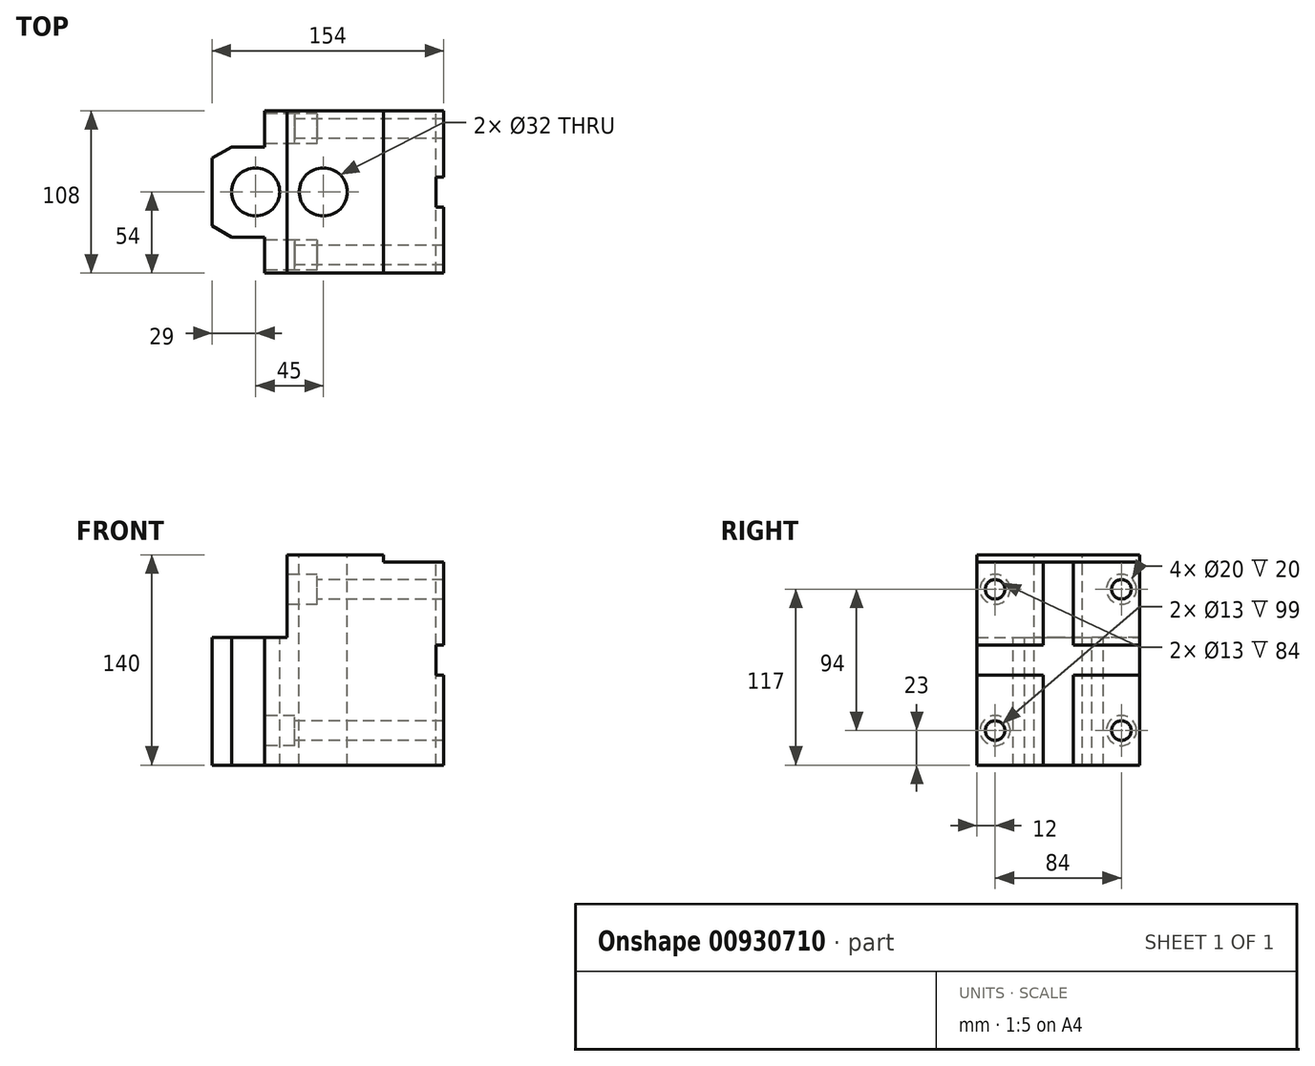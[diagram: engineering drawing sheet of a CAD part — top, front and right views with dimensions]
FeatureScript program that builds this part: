
annotation { "Feature Type Name" : "Feature", "Feature Type Description" : "" }
export const myFeature = defineFeature(function(context is Context, id is Id, definition is map)
    precondition{}
    {
        {
            var Q0;
            Q0=qCreatedBy(makeId("Right.planeOp"),FACE);
            var sketch = newSketch(context, id + "F0", { "sketchPlane" : qUnion([Q0])});
            skLineSegment(sketch, "E0.bottom", {"start": v(54, 70) * mm, "end": v(-54, 70) * mm});
            skLineSegment(sketch, "E0.top", {"start": v(54, -70) * mm, "end": v(-54, -70) * mm});
            skLineSegment(sketch, "E0.left", {"start": v(54, 70) * mm, "end": v(54, -70) * mm});
            skLineSegment(sketch, "E0.right", {"start": v(-54, 70) * mm, "end": v(-54, -70) * mm});
            skPoint(sketch, "E0.middle", {"position": v(0, 0) * mm});
            skSolve(sketch);
        }
        {
            var Q0;
            Q0 = qSketchRegion(id + "F0", true);
            extrude(context, id + "F1", {"entities" : qUnion([Q0]), "oppositeDirection" : true, "depth" : 154 * mm, "offsetDistance" : 25 * mm});
        }
        {
            var Q0;
            Q0=makeQuery(id+"F1.opExtrude","CAP_FACE",FACE,{"disambiguationData":[OSD([sQuery(id+"F0.wireOp",EDGE,"E0.bottom"),sQuery(id+"F0.wireOp",EDGE,"E0.top"),sQuery(id+"F0.wireOp",EDGE,"E0.left"),sQuery(id+"F0.wireOp",EDGE,"E0.right")])],"isStart":false});
            var sketch = newSketch(context, id + "F2", { "sketchPlane" : qUnion([Q0])});
            skCircle(sketch, "E1", {"center": v(-42, 47) * mm, "radius": 6.5 * mm});
            skCircle(sketch, "E2.MirrorC", {"center": v(42, 47) * mm, "radius": 6.5 * mm});
            skCircle(sketch, "E3.MirrorC", {"center": v(-42, -47) * mm, "radius": 6.5 * mm});
            skCircle(sketch, "E4.MirrorC", {"center": v(42, -47) * mm, "radius": 6.5 * mm});
            skSolve(sketch);
        }
        {
            var Q0;
            Q0 = qSketchRegion(id + "F2", true);
            extrude(context, id + "F3", {"entities" : qUnion([Q0]), "operationType" : NewBodyOperationType.REMOVE, "endBound" : BoundingType.THROUGH_ALL, "oppositeDirection" : true, "depth" : 25 * mm, "offsetDistance" : 25 * mm});
        }
        {
            var Q0;
            Q0=makeQuery(id+"F1.opExtrude","SWEPT_FACE",FACE,{"disambiguationData":[OSD([sQuery(id+"F0.wireOp",EDGE,"E0.top")])]});
            var sketch = newSketch(context, id + "F4", { "sketchPlane" : qUnion([Q0])});
            skCircle(sketch, "E5", {"center": v(-125, 0) * mm, "radius": 16 * mm});
            skCircle(sketch, "E6", {"center": v(-80, 0) * mm, "radius": 16 * mm});
            skSolve(sketch);
        }
        {
            var Q0;
            Q0 = qSketchRegion(id + "F4", true);
            extrude(context, id + "F5", {"entities" : qUnion([Q0]), "operationType" : NewBodyOperationType.REMOVE, "endBound" : BoundingType.THROUGH_ALL, "oppositeDirection" : true, "depth" : 25 * mm, "offsetDistance" : 25 * mm});
        }
        {
            var Q0;
            Q0=makeQuery(id+"F1.opExtrude","CAP_FACE",FACE,{"disambiguationData":[OSD([sQuery(id+"F0.wireOp",EDGE,"E0.bottom"),sQuery(id+"F0.wireOp",EDGE,"E0.top"),sQuery(id+"F0.wireOp",EDGE,"E0.left"),sQuery(id+"F0.wireOp",EDGE,"E0.right")])],"isStart":false});
            var sketch = newSketch(context, id + "F6", { "sketchPlane" : qUnion([Q0])});
            skLineSegment(sketch, "E7.bottom", {"start": v(-54, -70) * mm, "end": v(54, -70) * mm});
            skLineSegment(sketch, "E7.top", {"start": v(-54, -15) * mm, "end": v(54, -15) * mm});
            skLineSegment(sketch, "E7.left", {"start": v(-54, -70) * mm, "end": v(-54, -15) * mm});
            skLineSegment(sketch, "E7.right", {"start": v(54, -70) * mm, "end": v(54, -15) * mm});
            skSolve(sketch);
        }
        {
            var Q0;
            Q0 = qSketchRegion(id + "F6", true);
            extrude(context, id + "F7", {"entities" : qUnion([Q0]), "operationType" : NewBodyOperationType.REMOVE, "oppositeDirection" : true, "depth" : 50 * mm, "offsetDistance" : 25 * mm});
        }
        {
            var Q0;
            Q0=makeQuery(id+"F7.boolean.opBoolean","COPY",FACE,{"derivedFrom":makeQuery(id+"F7.opExtrude","SWEPT_FACE",FACE,{"disambiguationData":[OSD([sQuery(id+"F6.wireOp",EDGE,"E7.top")])]})});
            var sketch = newSketch(context, id + "F8", { "sketchPlane" : qUnion([Q0])});
            skLineSegment(sketch, "E8", {"start": v(-104, 54) * mm, "end": v(-119, 54) * mm});
            skLineSegment(sketch, "E9", {"start": v(-119, 54) * mm, "end": v(-119, 30) * mm});
            skLineSegment(sketch, "E10", {"start": v(-119, 30) * mm, "end": v(-141, 30) * mm});
            skLineSegment(sketch, "E11", {"start": v(-141, 30) * mm, "end": v(-154, 22.5) * mm});
            skLineSegment(sketch, "E12", {"start": v(-154, 22.5) * mm, "end": v(-154, 0) * mm});
            skLineSegment(sketch, "E13", {"start": v(-104, 54) * mm, "end": v(-104, 0) * mm});
            skLineSegment(sketch, "E14.MirrorCS", {"start": v(-154, -22.5) * mm, "end": v(-154, 0) * mm});
            skLineSegment(sketch, "E15.MirrorCS", {"start": v(-141, -30) * mm, "end": v(-154, -22.5) * mm});
            skLineSegment(sketch, "E16.MirrorCS", {"start": v(-119, -30) * mm, "end": v(-141, -30) * mm});
            skLineSegment(sketch, "E17.MirrorCS", {"start": v(-119, -54) * mm, "end": v(-119, -30) * mm});
            skLineSegment(sketch, "E18.MirrorCS", {"start": v(-104, -54) * mm, "end": v(-119, -54) * mm});
            skLineSegment(sketch, "E19.MirrorCS", {"start": v(-104, -54) * mm, "end": v(-104, 0) * mm});
            skSolve(sketch);
        }
        {
            var Q0;
            {var subQ5=sQuery(id+"F8.wireOp",EDGE,"E15.MirrorCS");Q0=makeQuery(id+"F8.imprint","IMPRINT",FACE,{"disambiguationData":[TD([[makeQuery(id+"F8.imprint","IMPRINT",EDGE,{"derivedFrom":subQ5}),1.0]])]});}
            var Q1;
            {var subQ4=sQuery(id+"F8.wireOp",EDGE,"E9");Q1=makeQuery(id+"F8.imprint","IMPRINT",FACE,{"disambiguationData":[TD([[makeQuery(id+"F8.imprint","IMPRINT",EDGE,{"derivedFrom":subQ4}),-1.0]])]});}
            extrude(context, id + "F9", {"entities" : qUnion([Q0, Q1]), "operationType" : NewBodyOperationType.REMOVE, "endBound" : BoundingType.THROUGH_ALL, "oppositeDirection" : true, "depth" : 25 * mm, "offsetDistance" : 25 * mm});
        }
        {
            var Q0;
            Q0=makeQuery(id+"F1.opExtrude","SWEPT_FACE",FACE,{"disambiguationData":[OSD([sQuery(id+"F0.wireOp",EDGE,"E0.top")])]});
            var sketch = newSketch(context, id + "F10", { "sketchPlane" : qUnion([Q0])});
            skLineSegment(sketch, "E20.bottom", {"start": v(0, 54) * mm, "end": v(-40, 54) * mm});
            skLineSegment(sketch, "E20.top", {"start": v(0, -54) * mm, "end": v(-40, -54) * mm});
            skLineSegment(sketch, "E20.left", {"start": v(0, 54) * mm, "end": v(0, -54) * mm});
            skLineSegment(sketch, "E20.right", {"start": v(-40, 54) * mm, "end": v(-40, -54) * mm});
            skSolve(sketch);
        }
        {
            var Q0;
            Q0 = qSketchRegion(id + "F10", true);
            extrude(context, id + "F11", {"entities" : qUnion([Q0]), "operationType" : NewBodyOperationType.REMOVE, "oppositeDirection" : true, "depth" : 5 * mm, "offsetDistance" : 25 * mm});
        }
        {
            var Q0;
            Q0=makeQuery(id+"F7.boolean.opBoolean","COPY",FACE,{"derivedFrom":makeQuery(id+"F7.opExtrude","CAP_FACE",FACE,{"disambiguationData":[OSD([sQuery(id+"F6.wireOp",EDGE,"E7.bottom"),sQuery(id+"F6.wireOp",EDGE,"E7.top"),sQuery(id+"F6.wireOp",EDGE,"E7.left"),sQuery(id+"F6.wireOp",EDGE,"E7.right")])],"isStart":false})});
            var sketch = newSketch(context, id + "F12", { "sketchPlane" : qUnion([Q0])});
            skCircle(sketch, "E21", {"center": v(-42, -47) * mm, "radius": 10 * mm});
            skCircle(sketch, "E22.MirrorC", {"center": v(42, -47) * mm, "radius": 10 * mm});
            skSolve(sketch);
        }
        {
            var Q0;
            Q0 = qSketchRegion(id + "F12", true);
            extrude(context, id + "F13", {"entities" : qUnion([Q0]), "operationType" : NewBodyOperationType.REMOVE, "oppositeDirection" : true, "depth" : 20 * mm, "offsetDistance" : 25 * mm});
        }
        {
            var Q0;
            Q0=makeQuery(id+"F9.boolean.opBoolean","COPY",FACE,{"derivedFrom":makeQuery(id+"F9.opExtrude","SWEPT_FACE",FACE,{"disambiguationData":[OSD([sQuery(id+"F8.wireOp",EDGE,"E17.MirrorCS")])]})});
            var sketch = newSketch(context, id + "F14", { "sketchPlane" : qUnion([Q0])});
            skCircle(sketch, "E23", {"center": v(-42, 47) * mm, "radius": 10 * mm});
            skCircle(sketch, "E24.MirrorC", {"center": v(42, 47) * mm, "radius": 10 * mm});
            skSolve(sketch);
        }
        {
            var Q0;
            Q0 = qSketchRegion(id + "F14", true);
            extrude(context, id + "F15", {"entities" : qUnion([Q0]), "operationType" : NewBodyOperationType.REMOVE, "oppositeDirection" : true, "depth" : 20 * mm, "offsetDistance" : 25 * mm});
        }
        {
            var Q0;
            Q0=makeQuery(id+"F1.opExtrude","CAP_FACE",FACE,{"disambiguationData":[OSD([sQuery(id+"F0.wireOp",EDGE,"E0.bottom"),sQuery(id+"F0.wireOp",EDGE,"E0.top"),sQuery(id+"F0.wireOp",EDGE,"E0.left"),sQuery(id+"F0.wireOp",EDGE,"E0.right")])],"isStart":true});
            var sketch = newSketch(context, id + "F16", { "sketchPlane" : qUnion([Q0])});
            skLineSegment(sketch, "E25.bottom", {"start": v(10, 70) * mm, "end": v(-10, 70) * mm});
            skLineSegment(sketch, "E25.top", {"start": v(10, -70) * mm, "end": v(-10, -70) * mm});
            skLineSegment(sketch, "E25.left", {"start": v(10, 70) * mm, "end": v(10, -70) * mm});
            skLineSegment(sketch, "E25.right", {"start": v(-10, 70) * mm, "end": v(-10, -70) * mm});
            skPoint(sketch, "E25.middle", {"position": v(0, 0) * mm});
            skLineSegment(sketch, "E26.bottom", {"start": v(54, 10) * mm, "end": v(-54, 10) * mm});
            skLineSegment(sketch, "E26.top", {"start": v(54, -10) * mm, "end": v(-54, -10) * mm});
            skLineSegment(sketch, "E26.left", {"start": v(54, 10) * mm, "end": v(54, -10) * mm});
            skLineSegment(sketch, "E26.right", {"start": v(-54, 10) * mm, "end": v(-54, -10) * mm});
            skSolve(sketch);
        }
        {
            var Q0;
            Q0 = qSketchRegion(id + "F16", true);
            extrude(context, id + "F17", {"entities" : qUnion([Q0]), "operationType" : NewBodyOperationType.REMOVE, "oppositeDirection" : true, "depth" : 5 * mm, "offsetDistance" : 25 * mm});
        }
        {
            var Q0;
            Q0=qCreatedBy(makeId("Top.planeOp"),FACE);
            var sketch = newSketch(context, id + "F18", { "sketchPlane" : qUnion([Q0])});
            skLineSegment(sketch, "E27", {"start": v(0, 0) * mm, "end": v(116.73, 0) * mm, "construction": true});
            skSolve(sketch);
        }
        {
            var Q0;
            Q0=makeQuery(id+"F1.opExtrude","SWEPT_BODY",BODY,{"disambiguationData":[OSD([sQuery(id+"F0.wireOp",EDGE,"E0.bottom"),sQuery(id+"F0.wireOp",EDGE,"E0.top"),sQuery(id+"F0.wireOp",EDGE,"E0.left"),sQuery(id+"F0.wireOp",EDGE,"E0.right")])]});
            var Q1;
            Q1=sQuery(id+"F18.wireOp",EDGE,"E27");
            transform(context, id + "F19", {"entities" : qUnion([Q0]), "transformType" : TransformType.ROTATION, "transformAxis" : qUnion([Q1]), "angle" : 180 * degree, "makeCopy" : false});
        }
    });
